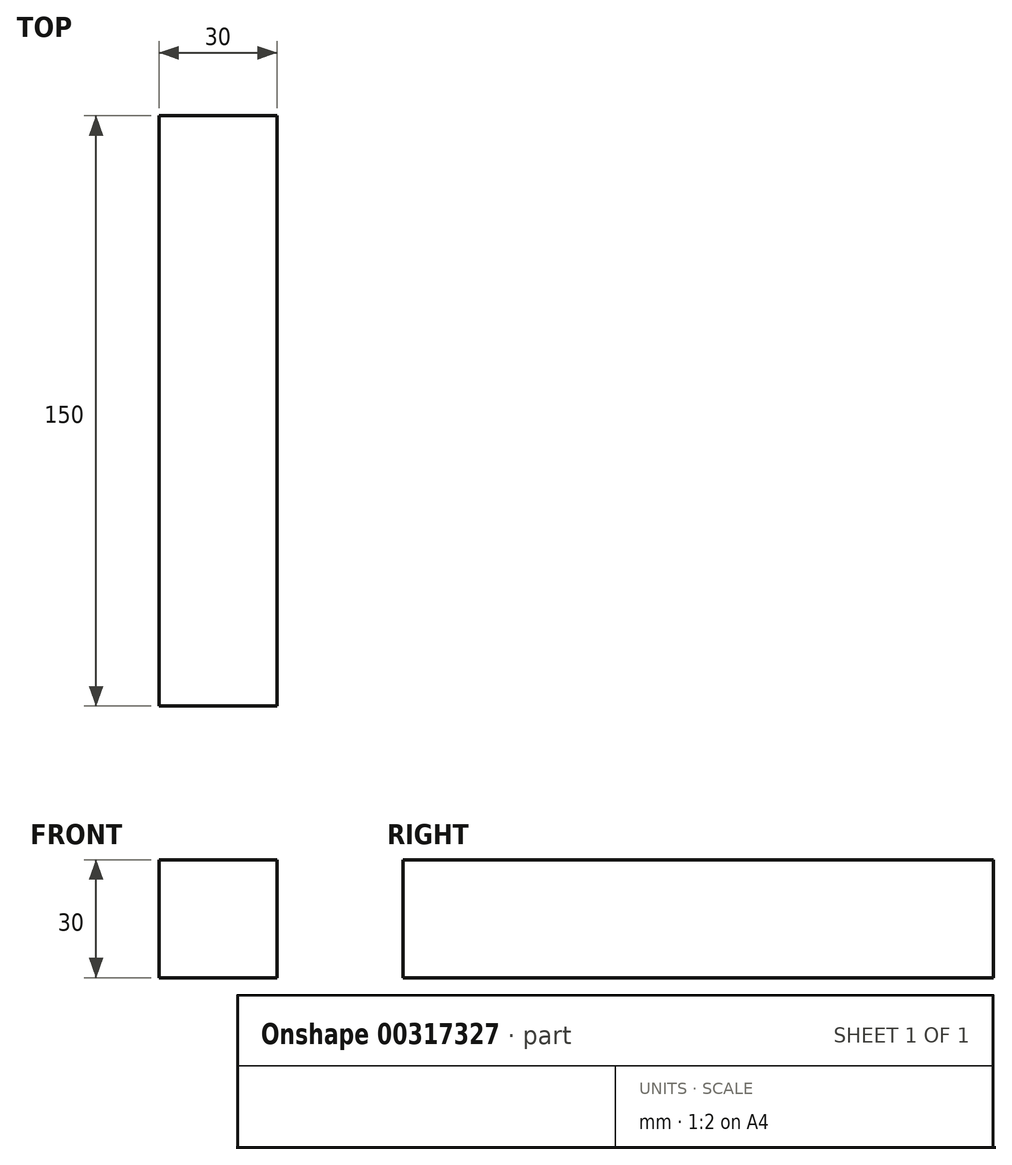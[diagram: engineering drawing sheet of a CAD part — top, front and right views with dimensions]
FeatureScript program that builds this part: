
annotation { "Feature Type Name" : "Feature", "Feature Type Description" : "" }
export const myFeature = defineFeature(function(context is Context, id is Id, definition is map)
    precondition{}
    {
        {
            var Q0;
            Q0=qCreatedBy(makeId("Front.planeOp"),FACE);
            var sketch = newSketch(context, id + "F0", { "sketchPlane" : qUnion([Q0])});
            skLineSegment(sketch, "E0.bottom", {"start": v(-15, 15) * mm, "end": v(15, 15) * mm});
            skLineSegment(sketch, "E0.top", {"start": v(-15, -15) * mm, "end": v(15, -15) * mm});
            skLineSegment(sketch, "E0.left", {"start": v(-15, 15) * mm, "end": v(-15, -15) * mm});
            skLineSegment(sketch, "E0.right", {"start": v(15, 15) * mm, "end": v(15, -15) * mm});
            skPoint(sketch, "E0.middle", {"position": v(0, 0) * mm});
            skSolve(sketch);
        }
        {
            var Q0;
            Q0 = qSketchRegion(id + "F0", true);
            extrude(context, id + "F1", {"entities" : qUnion([Q0]), "depth" : 150 * mm});
        }
    });
